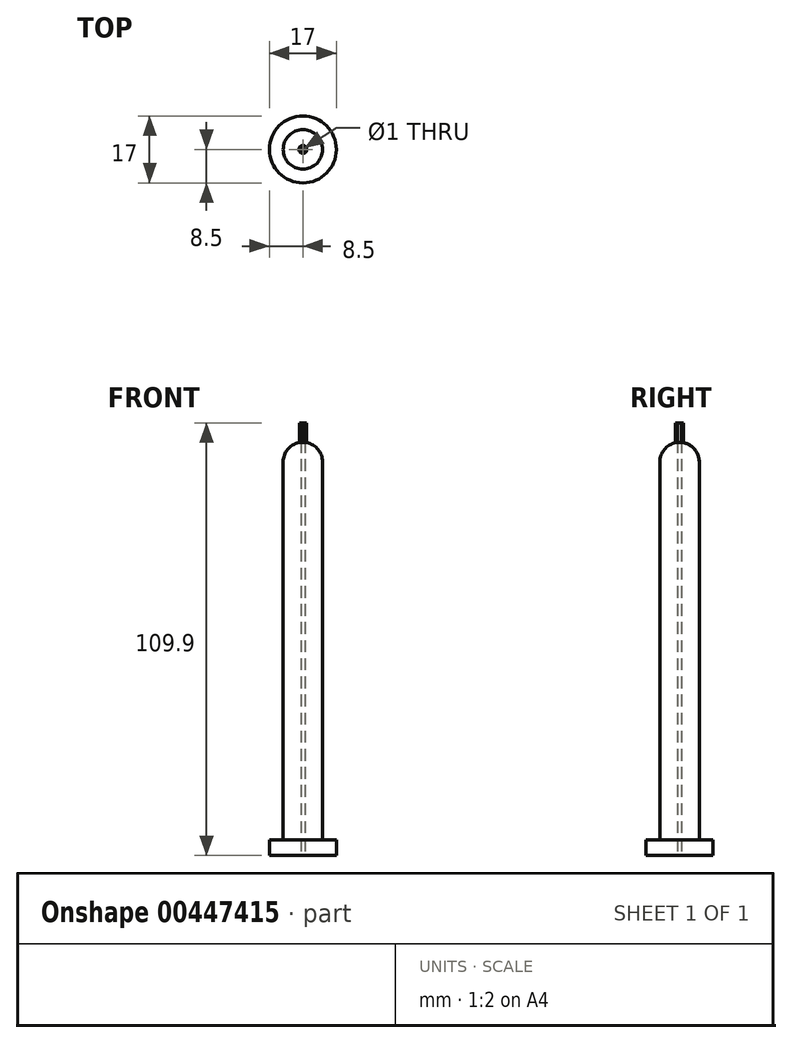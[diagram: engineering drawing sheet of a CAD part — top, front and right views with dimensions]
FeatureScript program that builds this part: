
annotation { "Feature Type Name" : "Feature", "Feature Type Description" : "" }
export const myFeature = defineFeature(function(context is Context, id is Id, definition is map)
    precondition{}
    {
        {
            var Q0;
            Q0=qCreatedBy(makeId("Top.planeOp"),FACE);
            var sketch = newSketch(context, id + "F0", { "sketchPlane" : qUnion([Q0])});
            skCircle(sketch, "E0", {"center": v(0, 0) * mm, "radius": 8.5 * mm});
            skSolve(sketch);
        }
        {
            var Q0;
            Q0=qSketchRegion(id+"F0",true);
            extrude(context, id + "F1", {"entities" : qUnion([Q0]), "depth" : 4 * mm});
        }
        {
            var Q0;
            Q0=qCreatedBy(makeId("Top.planeOp"),FACE);
            var sketch = newSketch(context, id + "F2", { "sketchPlane" : qUnion([Q0])});
            skCircle(sketch, "E1", {"center": v(0, 0) * mm, "radius": 5 * mm});
            skSolve(sketch);
        }
        {
            var Q0;
            Q0=qSketchRegion(id+"F2",true);
            extrude(context, id + "F3", {"entities" : qUnion([Q0]), "operationType" : NewBodyOperationType.ADD, "depth" : 100 * mm});
        }
        {
            var Q0;
            Q0=qCreatedBy(makeId("Right.planeOp"),FACE);
            var sketch = newSketch(context, id + "F4", { "sketchPlane" : qUnion([Q0])});
            skLineSegment(sketch, "E2", {"start": v(0, 100) * mm, "end": v(5, 100) * mm});
            skArc(sketch, "E3", {"start": v(5, 100) * mm, "mid": v(3.54, 103.54) * mm, "end": v(0, 105) * mm});
            skLineSegment(sketch, "E4", {"start": v(1, 104.9) * mm, "end": v(0, 104.9) * mm});
            skLineSegment(sketch, "E5", {"start": v(0, 107.19) * mm, "end": v(0, 100) * mm});
            skLineSegment(sketch, "E6", {"start": v(-1.55, -2.92) * mm, "end": v(3.45, -2.92) * mm});
            skArc(sketch, "E7", {"start": v(3.45, -2.92) * mm, "mid": v(1.99, 0.62) * mm, "end": v(-1.55, 2.08) * mm});
            skLineSegment(sketch, "E8", {"start": v(-0.55, 1.98) * mm, "end": v(-1.55, 1.98) * mm});
            skLineSegment(sketch, "E9", {"start": v(-1.55, 4.27) * mm, "end": v(-1.55, -2.92) * mm});
            skLineSegment(sketch, "E10", {"start": v(-0.77, 48.54) * mm, "end": v(4.23, 48.54) * mm});
            skArc(sketch, "E11", {"start": v(4.23, 48.54) * mm, "mid": v(2.76, 52.08) * mm, "end": v(-0.77, 53.54) * mm});
            skLineSegment(sketch, "E12", {"start": v(0.23, 53.44) * mm, "end": v(-0.77, 53.44) * mm});
            skLineSegment(sketch, "E13", {"start": v(-0.77, 55.73) * mm, "end": v(-0.77, 48.54) * mm});
            skLineSegment(sketch, "E14", {"start": v(-2.32, -54.38) * mm, "end": v(2.68, -54.38) * mm});
            skArc(sketch, "E15", {"start": v(2.68, -54.38) * mm, "mid": v(1.22, -50.84) * mm, "end": v(-2.32, -49.38) * mm});
            skLineSegment(sketch, "E16", {"start": v(-1.32, -49.48) * mm, "end": v(-2.32, -49.48) * mm});
            skLineSegment(sketch, "E17", {"start": v(-2.32, -47.2) * mm, "end": v(-2.32, -54.38) * mm});
            skSolve(sketch);
        }
        {
            var Q0;
            Q0=qCreatedBy(makeId("Right.planeOp"),FACE);
            var sketch = newSketch(context, id + "F5", { "sketchPlane" : qUnion([Q0])});
            skLineSegment(sketch, "E18", {"start": v(0, 86.28) * mm, "end": v(0, 91.28) * mm});
            skLineSegment(sketch, "E19", {"start": v(0, 91.28) * mm, "end": v(4.32, 86.28) * mm});
            skLineSegment(sketch, "E20", {"start": v(4.32, 86.28) * mm, "end": v(0, 86.28) * mm});
            skLineSegment(sketch, "E21", {"start": v(0, 105) * mm, "end": v(0, 100) * mm});
            skLineSegment(sketch, "E22", {"start": v(0, 100) * mm, "end": v(5, 100) * mm});
            skArc(sketch, "E23", {"start": v(5, 100) * mm, "mid": v(3.54, 103.54) * mm, "end": v(0, 105) * mm});
            skSolve(sketch);
        }
        {
            var Q0;
            {var subQ0=sQuery(id+"F4.wireOp",EDGE,"E2");Q0=makeQuery(id+"F4.imprint","IMPRINT",FACE,{"disambiguationData":[TD([[makeQuery(id+"F4.imprint","IMPRINT",EDGE,{"derivedFrom":subQ0}),1.0]])]});}
            var Q1;
            Q1=sQuery(id+"F5.wireOp",EDGE,"E21");
            revolve(context, id + "F6", {"operationType" : NewBodyOperationType.ADD, "entities" : qUnion([Q0]), "axis" : qUnion([Q1]), "revolveType" : RevolveType.FULL});
        }
        {
            var Q0;
            Q0=sQuery(id+"F4.wireOp",EDGE,"E4");
            cPlane(context, id + "F7", {"entities" : qUnion([Q0]), "cplaneType" : CPlaneType.LINE_ANGLE, "offset" : 25 * mm, "angle" : 0 * degree, "width" : 150 * mm, "height" : 150 * mm});
        }
        {
            var Q0;
            Q0=qCreatedBy(id+"F7.planeOp",FACE);
            var sketch = newSketch(context, id + "F8", { "sketchPlane" : qUnion([Q0])});
            skCircle(sketch, "E24.cCircle", {"center": v(0, 0) * mm, "radius": 0.87 * mm, "construction": true});
            skLineSegment(sketch, "E24.0", {"start": v(0.87, 0.5) * mm, "end": v(0.87, -0.5) * mm});
            skLineSegment(sketch, "E24.1", {"start": v(0.87, -0.5) * mm, "end": v(0, -1) * mm});
            skLineSegment(sketch, "E24.2", {"start": v(0, -1) * mm, "end": v(-0.87, -0.5) * mm});
            skLineSegment(sketch, "E24.3", {"start": v(-0.87, -0.5) * mm, "end": v(-0.87, 0.5) * mm});
            skLineSegment(sketch, "E24.4", {"start": v(-0.87, 0.5) * mm, "end": v(0, 1) * mm});
            skLineSegment(sketch, "E24.5", {"start": v(0, 1) * mm, "end": v(0.87, 0.5) * mm});
            skPoint(sketch, "E24.0.midPoint", {"position": v(0.87, 0) * mm});
            skSolve(sketch);
        }
        {
            var Q0;
            Q0=makeQuery(id+"F8.imprint","IMPRINT",FACE,{"disambiguationData":[TD([[makeQuery(id+"F8.imprint","IMPRINT",EDGE,{"derivedFrom":sQuery(id+"F8.wireOp",EDGE,"E24.0")}),-1.0]])]});
            extrude(context, id + "F9", {"entities" : qUnion([Q0]), "operationType" : NewBodyOperationType.ADD, "oppositeDirection" : true, "depth" : 5 * mm});
        }
        {
            var Q0;
            Q0=makeQuery(id+"F1.opExtrude","CAP_FACE",FACE,{"disambiguationData":[OSD([sQuery(id+"F0.wireOp",EDGE,"E0")])],"isStart":true});
            var sketch = newSketch(context, id + "F10", { "sketchPlane" : qUnion([Q0])});
            skCircle(sketch, "E25", {"center": v(0, 0) * mm, "radius": 0.5 * mm});
            skSolve(sketch);
        }
        {
            var Q0;
            Q0 = qSketchRegion(id + "F10", true);
            extrude(context, id + "F11", {"entities" : qUnion([Q0]), "operationType" : NewBodyOperationType.REMOVE, "oppositeDirection" : true, "depth" : 117.5 * mm});
        }
    });
